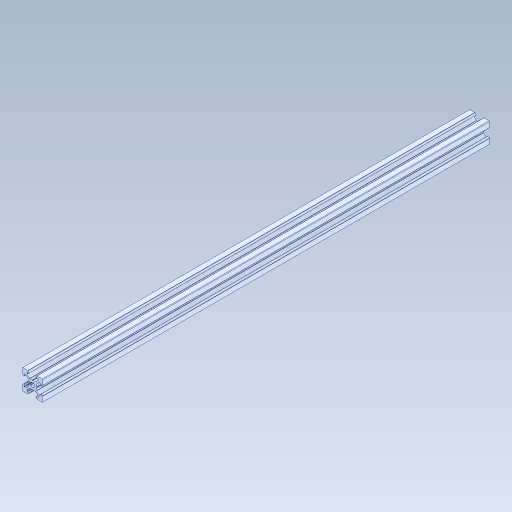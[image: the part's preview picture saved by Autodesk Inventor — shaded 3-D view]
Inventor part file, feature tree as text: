
AUTODESK INVENTOR PART (.ipt)
format: ipt  version: 2023 (Build 270158000, 158)  size: 501,248 bytes
history: mixed  units: in
note: dims shown in document units (in); Inventor stores cm internally (conversion verified against a paired STEP export)
features: other x3, extrude x1, sketch x1, projected_geometry x1, imported_body x1
ambient origin geometry x8: Origin, YZ Plane, XZ Plane, XY Plane, X Axis, Y Axis, Z Axis, Center Point
bodies: Solid1 (imported_parasolid)
feature tree (7):
  other  "Annotations"
  other  "Boss-Extrude1"
  extrude  "Extrusion1"  Depth=0.106in
  sketch  "Sketch2"  dims[d5=0.0787in d6=0.0in d0=0.106in d1=0.114in d2=17.3228in]
  projected_geometry  "Projected Loop1"
  other  "Linear Dimension 1"
  imported_body  NMx_Import_Brep_tag  [imported B-rep: ~114 faces, bbox_mm=[20.0, 20.0, 438.0]]
